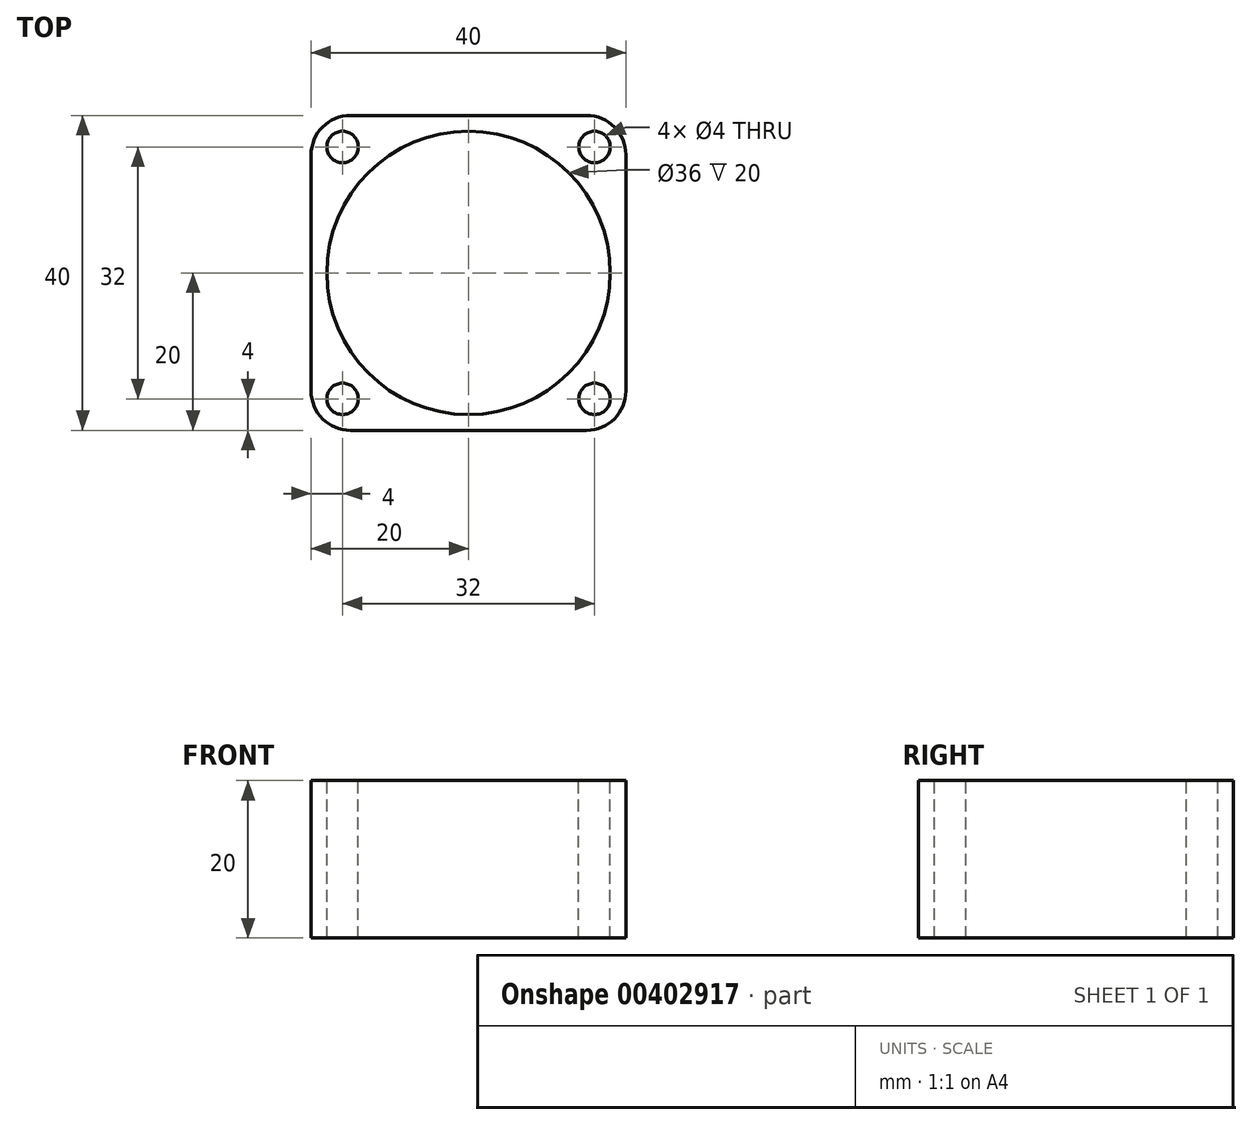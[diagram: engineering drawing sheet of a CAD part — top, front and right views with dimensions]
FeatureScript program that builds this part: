
annotation { "Feature Type Name" : "Feature", "Feature Type Description" : "" }
export const myFeature = defineFeature(function(context is Context, id is Id, definition is map)
    precondition{}
    {
        {
            var Q0;
            Q0=qCreatedBy(makeId("Top.planeOp"),FACE);
            var sketch = newSketch(context, id + "F0", { "sketchPlane" : qUnion([Q0])});
            skLineSegment(sketch, "E0.bottom", {"start": v(0, 0) * mm, "end": v(40, 0) * mm});
            skLineSegment(sketch, "E0.top", {"start": v(0, 40) * mm, "end": v(40, 40) * mm});
            skLineSegment(sketch, "E0.left", {"start": v(0, 0) * mm, "end": v(0, 40) * mm});
            skLineSegment(sketch, "E0.right", {"start": v(40, 0) * mm, "end": v(40, 40) * mm});
            skSolve(sketch);
        }
        {
            var Q0;
            Q0 = qSketchRegion(id + "F0", true);
            extrude(context, id + "F1", {"entities" : qUnion([Q0]), "depth" : 20 * mm, "offsetDistance" : 25 * mm});
        }
        {
            var Q0;
            Q0=makeQuery(id+"F1.opExtrude","CAP_FACE",FACE,{"disambiguationData":[OSD([sQuery(id+"F0.wireOp",EDGE,"E0.bottom"),sQuery(id+"F0.wireOp",EDGE,"E0.top"),sQuery(id+"F0.wireOp",EDGE,"E0.left"),sQuery(id+"F0.wireOp",EDGE,"E0.right")])],"isStart":false});
            var sketch = newSketch(context, id + "F2", { "sketchPlane" : qUnion([Q0])});
            skCircle(sketch, "E1", {"center": v(4, 36) * mm, "radius": 2 * mm});
            skCircle(sketch, "E2", {"center": v(36, 36) * mm, "radius": 2 * mm});
            skCircle(sketch, "E3", {"center": v(36, 4) * mm, "radius": 2 * mm});
            skCircle(sketch, "E4", {"center": v(4, 4) * mm, "radius": 2 * mm});
            skSolve(sketch);
        }
        {
            var Q0;
            Q0 = qSketchRegion(id + "F2", true);
            extrude(context, id + "F3", {"entities" : qUnion([Q0]), "operationType" : NewBodyOperationType.REMOVE, "oppositeDirection" : true, "depth" : 25 * mm, "offsetDistance" : 25 * mm});
        }
        {
            var Q0;
            Q0=makeQuery(id+"F1.opExtrude","CAP_FACE",FACE,{"disambiguationData":[OSD([sQuery(id+"F0.wireOp",EDGE,"E0.bottom"),sQuery(id+"F0.wireOp",EDGE,"E0.top"),sQuery(id+"F0.wireOp",EDGE,"E0.left"),sQuery(id+"F0.wireOp",EDGE,"E0.right")])],"isStart":false});
            var sketch = newSketch(context, id + "F4", { "sketchPlane" : qUnion([Q0])});
            skCircle(sketch, "E5", {"center": v(20, 20) * mm, "radius": 18 * mm});
            skPoint(sketch, "E5.centerSnap0", {"position": v(0, 20) * mm});
            skPoint(sketch, "E5.centerSnap1", {"position": v(20, 40) * mm});
            skSolve(sketch);
        }
        {
            var Q0;
            Q0 = qSketchRegion(id + "F4", true);
            extrude(context, id + "F5", {"entities" : qUnion([Q0]), "operationType" : NewBodyOperationType.REMOVE, "oppositeDirection" : true, "depth" : 25 * mm, "offsetDistance" : 25 * mm});
        }
        {
            var Q0;
            Q0=makeQuery(id+"F1.opExtrude","SWEPT_EDGE",EDGE,{"disambiguationData":[OSD([sQuery(id+"F0.wireOp",EDGE,"E0.bottom"),sQuery(id+"F0.wireOp",EDGE,"E0.left")])]});
            var Q1;
            Q1=makeQuery(id+"F1.opExtrude","SWEPT_EDGE",EDGE,{"disambiguationData":[OSD([sQuery(id+"F0.wireOp",EDGE,"E0.top"),sQuery(id+"F0.wireOp",EDGE,"E0.left")])]});
            var Q2;
            Q2=makeQuery(id+"F1.opExtrude","SWEPT_EDGE",EDGE,{"disambiguationData":[OSD([sQuery(id+"F0.wireOp",EDGE,"E0.top"),sQuery(id+"F0.wireOp",EDGE,"E0.right")])]});
            var Q3;
            Q3=makeQuery(id+"F1.opExtrude","SWEPT_EDGE",EDGE,{"disambiguationData":[OSD([sQuery(id+"F0.wireOp",EDGE,"E0.bottom"),sQuery(id+"F0.wireOp",EDGE,"E0.right")])]});
            fillet(context, id + "F6", {"entities" : qUnion([Q0, Q1, Q2, Q3]), "radius" : 5 * mm, "tangentPropagation" : true, "allowEdgeOverflow" : false});
        }
    });
